# Revit family: Shower-Outlet-Caroma Titan-Right Angle Wall1
name_source: partatom
category: Plumbing Fixtures
revit_build: Autodesk Revit 2013 (Build: 20121003_2115(x64)
units: mm (PartAtom-declared; Revit-internal decimal feet)

## types (2) — shared parameters
Assembly Code = C1030210
CW Connection = Yes
CWFU = 2.37
Connector Radius = 10 mm  [stored 0.0328084 ft]
Default Elevation = 2100 mm
HW Connection = Yes
HWFU = 2.37
Manufacturer = GWA Bathrooms & Kitchens
Model = 99021SS
Type Comments = Caroma Titan Wall Shower Arm Right Angle
URL = http://www.caroma.com.au
Vent Connection = No
Waste Connection = No
zero-valued in all types: Cost

## per-type parameters (varying)
| type | Head Size | Material_ANZRS |
| 200mm Head | Shower-Head-Caroma Titan : 200mm | Metal-Stainless Steel-Polished-Caroma |
| 300mm Head | Shower-Head-Caroma Titan : 300mm | Metal-Chrome-Caroma |

note: [stored X ft] marks values corroborated as IEEE doubles in the binary element streams (Revit-internal decimal feet)

## geometry (parser evidence)
native form markers: Blend x8, Sweep x3
no freeform markers — native parametric forms only
